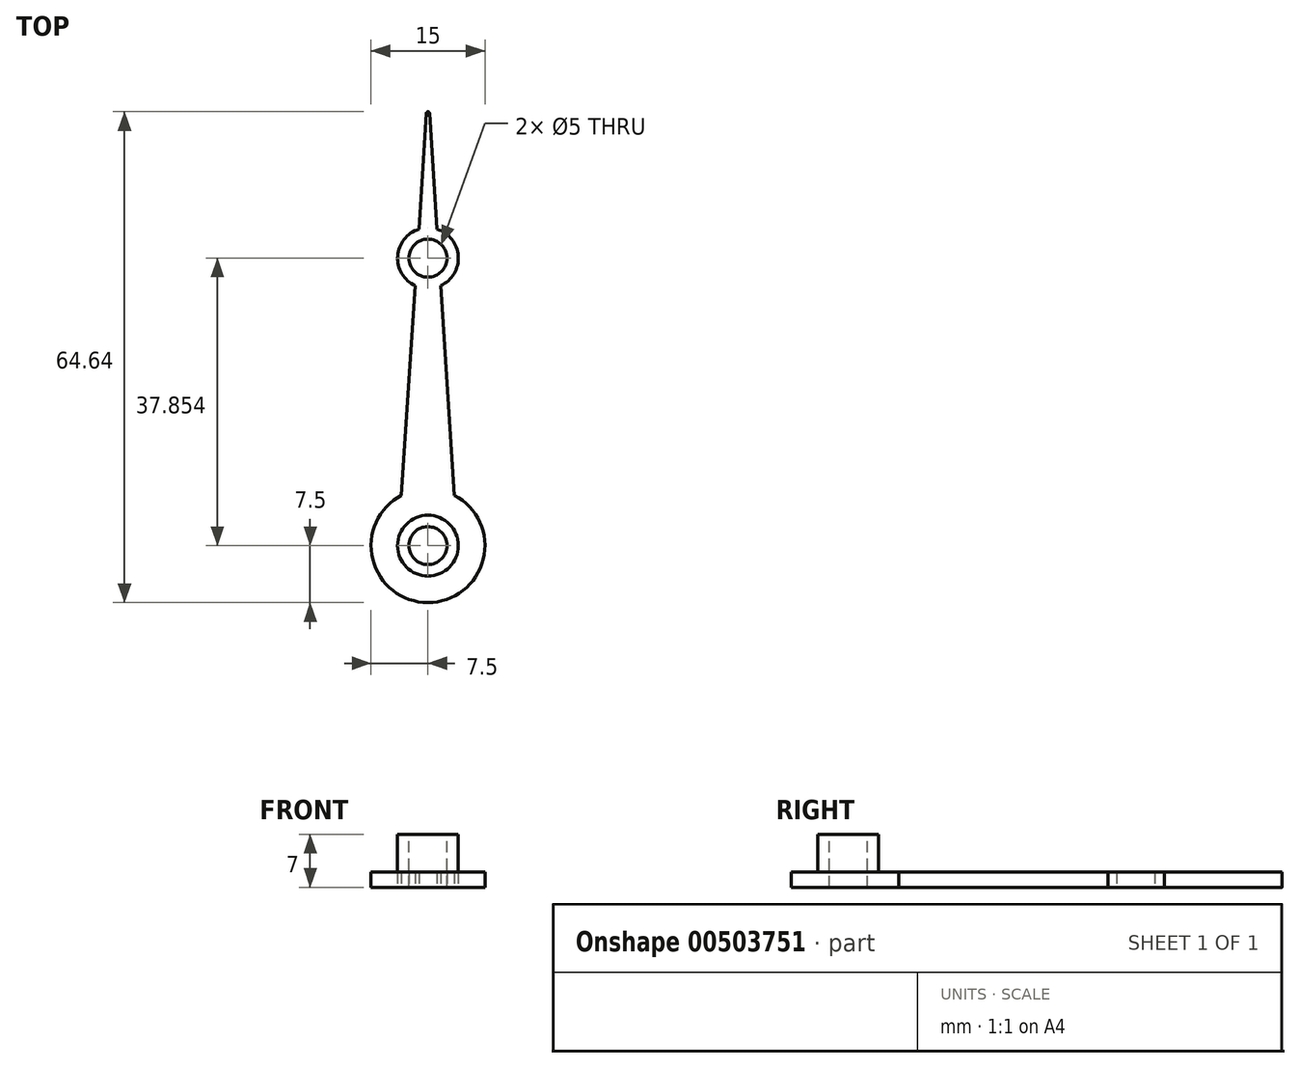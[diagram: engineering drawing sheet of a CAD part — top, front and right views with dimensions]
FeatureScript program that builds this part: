
annotation { "Feature Type Name" : "Feature", "Feature Type Description" : "" }
export const myFeature = defineFeature(function(context is Context, id is Id, definition is map)
    precondition{}
    {
        {
            var Q0;
            Q0=qCreatedBy(makeId("Top.planeOp"),FACE);
            var sketch = newSketch(context, id + "F0", { "sketchPlane" : qUnion([Q0])});
            skArc(sketch, "E0", {"start": v(-3.5, 6.64) * mm, "mid": v(0, -7.5) * mm, "end": v(3.5, 6.64) * mm});
            skCircle(sketch, "E1", {"center": v(0, 0) * mm, "radius": 60 * mm, "construction": true});
            skLineSegment(sketch, "E2", {"start": v(-0.2, 56.95) * mm, "end": v(-1.2, 41.67) * mm});
            skLineSegment(sketch, "E3.MirrorCS", {"start": v(0.2, 56.95) * mm, "end": v(1.2, 41.67) * mm});
            skPoint(sketch, "E4.visualSharp", {"position": v(0, 60) * mm});
            skArc(sketch, "E4.filletArc", {"start": v(0.2, 56.95) * mm, "mid": v(0, 57.14) * mm, "end": v(-0.2, 56.95) * mm});
            skArc(sketch, "E5", {"start": v(1.69, 34.23) * mm, "mid": v(4, 38.11) * mm, "end": v(1.2, 41.67) * mm});
            skLineSegment(sketch, "E6.trimOffspring", {"start": v(-1.69, 34.23) * mm, "end": v(-3.5, 6.64) * mm});
            skLineSegment(sketch, "E7.trimOffspring", {"start": v(1.69, 34.23) * mm, "end": v(3.5, 6.64) * mm});
            skArc(sketch, "E8.trimOffspring", {"start": v(-1.2, 41.67) * mm, "mid": v(-4, 38.11) * mm, "end": v(-1.69, 34.23) * mm});
            skCircle(sketch, "E9", {"center": v(0, 37.85) * mm, "radius": 2.5 * mm});
            skSolve(sketch);
        }
        {
            var Q0;
            Q0 = qSketchRegion(id + "F0", true);
            extrude(context, id + "F1", {"entities" : qUnion([Q0]), "depth" : 2 * mm, "offsetDistance" : 25 * mm});
        }
        {
            var Q0;
            Q0=makeQuery(id+"F1.opExtrude","CAP_FACE",FACE,{"disambiguationData":[OSD([sQuery(id+"F0.wireOp",EDGE,"E0"),sQuery(id+"F0.wireOp",EDGE,"E2"),sQuery(id+"F0.wireOp",EDGE,"E3.MirrorCS"),sQuery(id+"F0.wireOp",EDGE,"E4.filletArc"),sQuery(id+"F0.wireOp",EDGE,"E5"),sQuery(id+"F0.wireOp",EDGE,"E6.trimOffspring"),sQuery(id+"F0.wireOp",EDGE,"E7.trimOffspring"),sQuery(id+"F0.wireOp",EDGE,"E8.trimOffspring"),sQuery(id+"F0.wireOp",EDGE,"E9")])],"isStart":false});
            var sketch = newSketch(context, id + "F2", { "sketchPlane" : qUnion([Q0])});
            skCircle(sketch, "E10", {"center": v(0, 0) * mm, "radius": 4 * mm});
            skSolve(sketch);
        }
        {
            var Q0;
            Q0 = qSketchRegion(id + "F2", true);
            extrude(context, id + "F3", {"entities" : qUnion([Q0]), "operationType" : NewBodyOperationType.ADD, "depth" : 5 * mm, "offsetDistance" : 25 * mm});
        }
        {
            var Q0;
            Q0=makeQuery(id+"F3.opExtrude","CAP_FACE",FACE,{"disambiguationData":[OSD([sQuery(id+"F2.wireOp",EDGE,"E10")])],"isStart":false});
            var sketch = newSketch(context, id + "F4", { "sketchPlane" : qUnion([Q0])});
            skCircle(sketch, "E11", {"center": v(0, 0) * mm, "radius": 2.5 * mm});
            skSolve(sketch);
        }
        {
            var Q0;
            Q0 = qSketchRegion(id + "F4", true);
            extrude(context, id + "F5", {"entities" : qUnion([Q0]), "operationType" : NewBodyOperationType.REMOVE, "endBound" : BoundingType.THROUGH_ALL, "oppositeDirection" : true, "depth" : 25 * mm, "offsetDistance" : 25 * mm});
        }
    });
